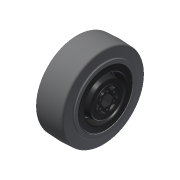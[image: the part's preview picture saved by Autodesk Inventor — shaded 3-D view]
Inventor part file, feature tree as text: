
AUTODESK INVENTOR PART (.ipt)
format: ipt  version: 2015 (Build 190159000, 159)  size: 2,771,968 bytes
history: native  units: in
note: dims shown in document units (in); Inventor stores cm internally (conversion verified against a paired STEP export)
features: boolean_combine x1, other x1, revolve x1, imported_body x1, sketch x1
ambient origin geometry x8: Origin, YZ Plane, XZ Plane, XY Plane, X Axis, Y Axis, Z Axis, Center Point
bodies: Body1 (feature_tree)
feature tree (5):
  boolean_combine  "Combine1"
  other  "217-4052-STEP-201410301"
  revolve  "Revolution1"  [1 undecoded]
  imported_body  "Base1"
  sketch  "Sketch1"  dims[d0=90.0deg]
note: 1 required parameter value undecoded (feature->parameter linkage not recoverable at this tier; creation-order binding heuristic only, values carry confidence <= 0.55)
